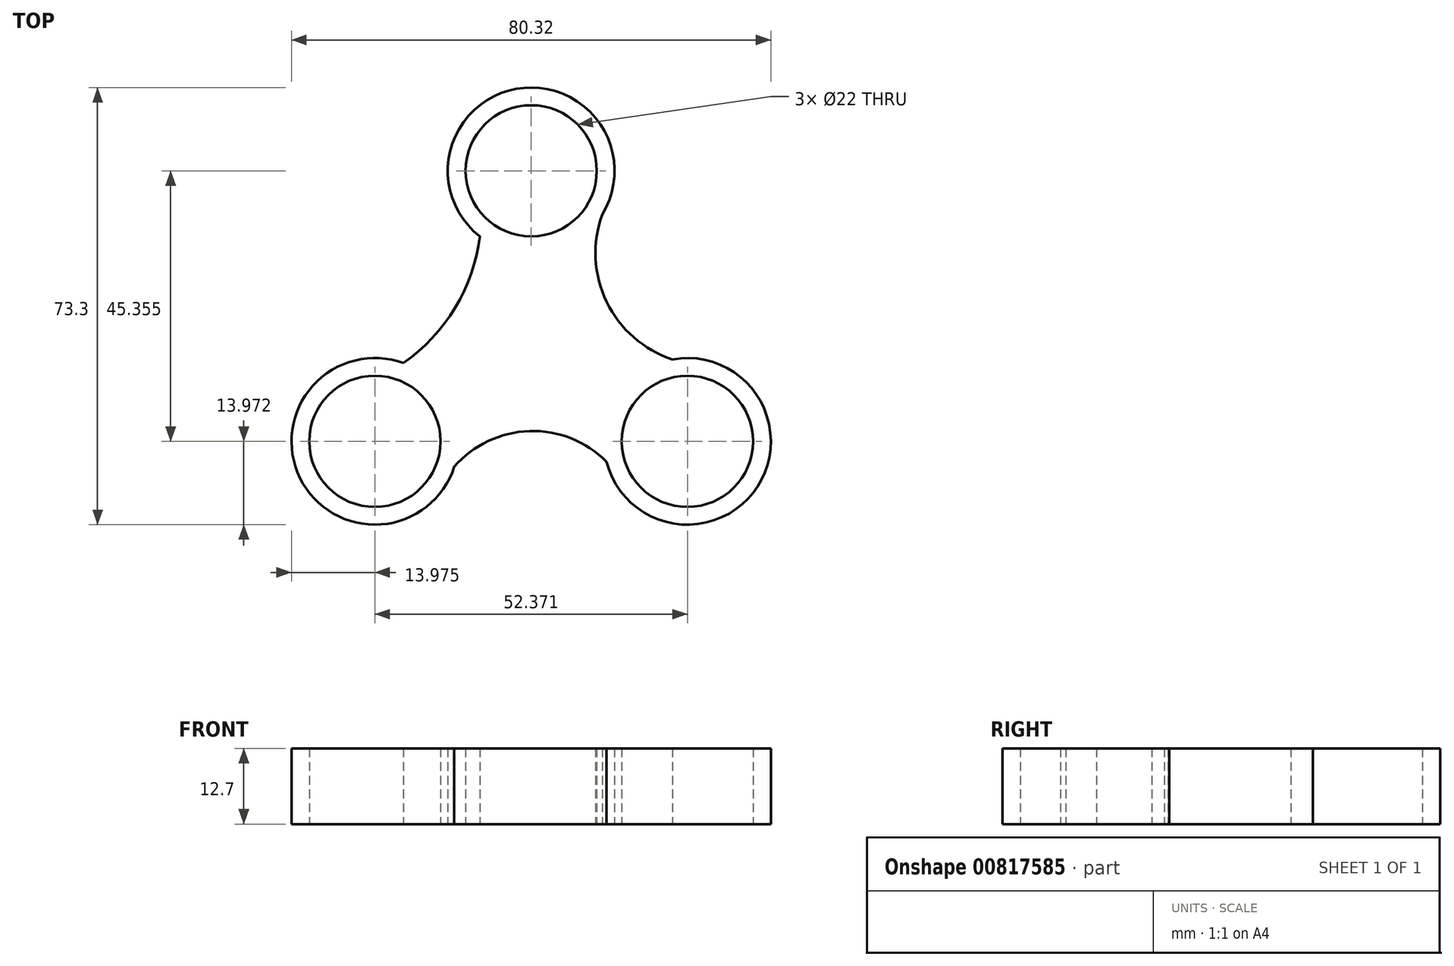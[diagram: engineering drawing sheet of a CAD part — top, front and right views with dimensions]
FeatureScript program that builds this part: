
annotation { "Feature Type Name" : "Feature", "Feature Type Description" : "" }
export const myFeature = defineFeature(function(context is Context, id is Id, definition is map)
    precondition{}
    {
        {
            var Q0;
            Q0=qCreatedBy(makeId("Top.planeOp"),FACE);
            var sketch = newSketch(context, id + "F0", { "sketchPlane" : qUnion([Q0])});
            skCircle(sketch, "E0", {"center": v(0, 0) * mm, "radius": 44.45 * mm});
            skCircle(sketch, "E1", {"center": v(0, 0) * mm, "radius": 11 * mm});
            skCircle(sketch, "E2", {"center": v(0, 30.24) * mm, "radius": 11 * mm});
            skCircle(sketch, "E3.1.0", {"center": v(-26.19, -15.12) * mm, "radius": 11 * mm});
            skCircle(sketch, "E3.2.0", {"center": v(26.19, -15.12) * mm, "radius": 11 * mm});
            skCircle(sketch, "E4", {"center": v(0, 30.24) * mm, "radius": 13.97 * mm});
            skCircle(sketch, "E5", {"center": v(-26.19, -15.12) * mm, "radius": 13.97 * mm});
            skCircle(sketch, "E6", {"center": v(26.19, -15.12) * mm, "radius": 13.97 * mm});
            skCircle(sketch, "E7", {"center": v(0, 0) * mm, "radius": 13.97 * mm});
            skArc(sketch, "E8", {"start": v(-21.4, -2) * mm, "mid": v(-12.76, 7.26) * mm, "end": v(-8.58, 19.2) * mm});
            skArc(sketch, "E9", {"start": v(12.64, -18.54) * mm, "mid": v(-0.3, -13.4) * mm, "end": v(-12.88, -19.37) * mm});
            skArc(sketch, "E10", {"start": v(11.9, 22.92) * mm, "mid": v(12.64, 8.28) * mm, "end": v(23.65, -1.38) * mm});
            skSolve(sketch);
        }
        {
            var Q0;
            Q0=makeQuery(id+"F0.imprint","IMPRINT",FACE,{"disambiguationData":[TD([[makeQuery(id+"F0.imprint","IMPRINT",EDGE,{"derivedFrom":sQuery(id+"F0.wireOp",EDGE,"E3.1.0")}),-1.0]])]});
            var Q1;
            {var subQ7=sQuery(id+"F0.wireOp",EDGE,"E8");Q1=makeQuery(id+"F0.imprint","IMPRINT",FACE,{"disambiguationData":[TD([[makeQuery(id+"F0.imprint","IMPRINT",EDGE,{"derivedFrom":subQ7}),-1.0]])]});}
            var Q2;
            Q2=makeQuery(id+"F0.imprint","IMPRINT",FACE,{"disambiguationData":[TD([[makeQuery(id+"F0.imprint","IMPRINT",EDGE,{"derivedFrom":sQuery(id+"F0.wireOp",EDGE,"E1")}),1.0]])]});
            var Q3;
            Q3=makeQuery(id+"F0.imprint","IMPRINT",FACE,{"disambiguationData":[TD([[makeQuery(id+"F0.imprint","IMPRINT",EDGE,{"derivedFrom":sQuery(id+"F0.wireOp",EDGE,"E3.2.0")}),-1.0]])]});
            var Q4;
            Q4=makeQuery(id+"F0.imprint","IMPRINT",FACE,{"disambiguationData":[TD([[makeQuery(id+"F0.imprint","IMPRINT",EDGE,{"derivedFrom":sQuery(id+"F0.wireOp",EDGE,"E1")}),-1.0]])]});
            var Q5;
            Q5=makeQuery(id+"F0.imprint","IMPRINT",FACE,{"disambiguationData":[TD([[makeQuery(id+"F0.imprint","IMPRINT",EDGE,{"derivedFrom":sQuery(id+"F0.wireOp",EDGE,"E2")}),-1.0]])]});
            extrude(context, id + "F1", {"entities" : qUnion([Q0, Q1, Q2, Q3, Q4, Q5]), "depth" : 12.7 * mm, "offsetDistance" : 25.4 * mm});
        }
    });
